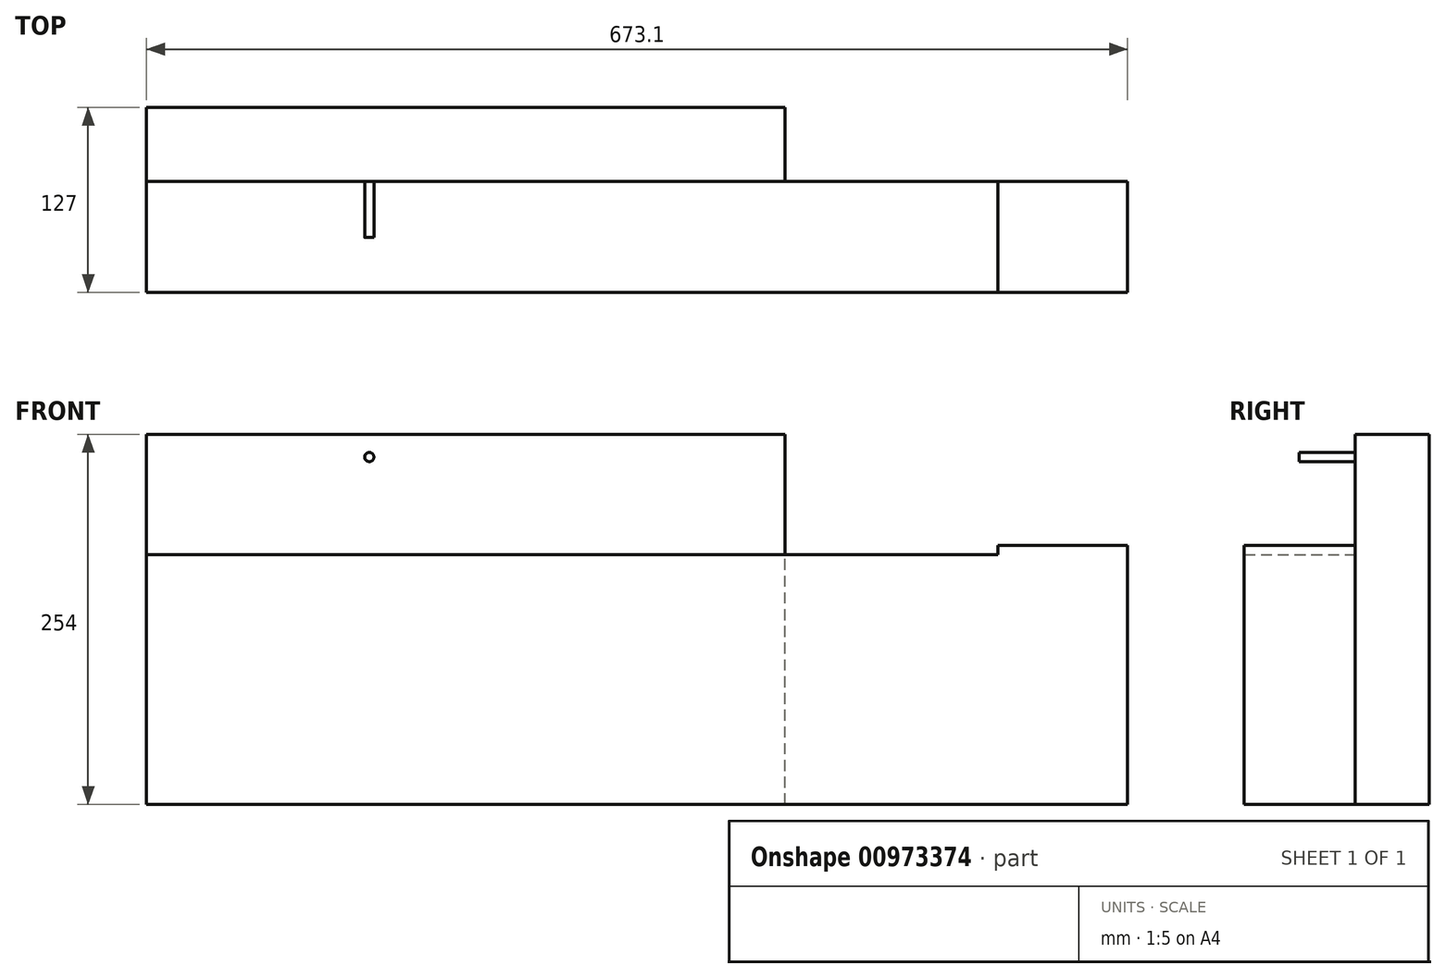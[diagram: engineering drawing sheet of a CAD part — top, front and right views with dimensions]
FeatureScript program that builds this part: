
annotation { "Feature Type Name" : "Feature", "Feature Type Description" : "" }
export const myFeature = defineFeature(function(context is Context, id is Id, definition is map)
    precondition{}
    {
        {
            var Q0;
            Q0=qCreatedBy(makeId("Right.planeOp"),FACE);
            var sketch = newSketch(context, id + "F0", { "sketchPlane" : qUnion([Q0])});
            skLineSegment(sketch, "E0.bottom", {"start": v(-63.5, -127) * mm, "end": v(63.5, -127) * mm});
            skLineSegment(sketch, "E0.top", {"start": v(12.7, 127) * mm, "end": v(63.5, 127) * mm});
            skLineSegment(sketch, "E0.right", {"start": v(63.5, -127) * mm, "end": v(63.5, 127) * mm});
            skPoint(sketch, "E0.middle", {"position": v(0, 0) * mm});
            skLineSegment(sketch, "E1", {"start": v(12.7, 127) * mm, "end": v(12.7, 44.45) * mm});
            skLineSegment(sketch, "E2", {"start": v(12.7, 44.45) * mm, "end": v(-63.5, 44.45) * mm});
            skLineSegment(sketch, "E3", {"start": v(-63.5, 44.45) * mm, "end": v(-63.5, -127) * mm});
            skSolve(sketch);
        }
        {
            var Q0;
            Q0 = qSketchRegion(id + "F0", true);
            extrude(context, id + "F1", {"entities" : qUnion([Q0]), "depth" : 673.1 * mm, "offsetDistance" : 25.4 * mm});
        }
        {
            var Q0;
            Q0=makeQuery(id+"F1.opExtrude","SWEPT_FACE",FACE,{"disambiguationData":[OSD([sQuery(id+"F0.wireOp",EDGE,"E0.top")])]});
            var sketch = newSketch(context, id + "F2", { "sketchPlane" : qUnion([Q0])});
            skLineSegment(sketch, "E4.bottom", {"start": v(673.1, 12.7) * mm, "end": v(438.15, 12.7) * mm});
            skLineSegment(sketch, "E4.top", {"start": v(673.1, 63.5) * mm, "end": v(438.15, 63.5) * mm});
            skLineSegment(sketch, "E4.left", {"start": v(673.1, 12.7) * mm, "end": v(673.1, 63.5) * mm});
            skLineSegment(sketch, "E4.right", {"start": v(438.15, 12.7) * mm, "end": v(438.15, 63.5) * mm});
            skSolve(sketch);
        }
        {
            var Q0;
            Q0 = qSketchRegion(id + "F2", true);
            extrude(context, id + "F3", {"entities" : qUnion([Q0]), "operationType" : NewBodyOperationType.REMOVE, "endBound" : BoundingType.THROUGH_ALL, "oppositeDirection" : true, "depth" : 25.4 * mm, "offsetDistance" : 25.4 * mm});
        }
        {
            var Q0;
            Q0=makeQuery(id+"F1.opExtrude","SWEPT_FACE",FACE,{"disambiguationData":[OSD([sQuery(id+"F0.wireOp",EDGE,"E2")])]});
            var sketch = newSketch(context, id + "F4", { "sketchPlane" : qUnion([Q0])});
            skLineSegment(sketch, "E5.bottom", {"start": v(673.1, -63.5) * mm, "end": v(584.2, -63.5) * mm});
            skLineSegment(sketch, "E5.top", {"start": v(673.1, 12.7) * mm, "end": v(584.2, 12.7) * mm});
            skLineSegment(sketch, "E5.left", {"start": v(673.1, -63.5) * mm, "end": v(673.1, 12.7) * mm});
            skLineSegment(sketch, "E5.right", {"start": v(584.2, -63.5) * mm, "end": v(584.2, 12.7) * mm});
            skSolve(sketch);
        }
        {
            var Q0;
            Q0 = qSketchRegion(id + "F4", true);
            extrude(context, id + "F5", {"entities" : qUnion([Q0]), "operationType" : NewBodyOperationType.ADD, "depth" : 6.35 * mm, "offsetDistance" : 25.4 * mm});
        }
        {
            var Q0;
            Q0=makeQuery(id+"F1.opExtrude","SWEPT_FACE",FACE,{"disambiguationData":[OSD([sQuery(id+"F0.wireOp",EDGE,"E1")])]});
            var sketch = newSketch(context, id + "F6", { "sketchPlane" : qUnion([Q0])});
            skCircle(sketch, "E6", {"center": v(152.78, 111.48) * mm, "radius": 3.18 * mm});
            skSolve(sketch);
        }
        {
            var Q0;
            Q0 = qSketchRegion(id + "F6", true);
            extrude(context, id + "F7", {"entities" : qUnion([Q0]), "operationType" : NewBodyOperationType.ADD, "depth" : 38.53 * mm, "offsetDistance" : 25.4 * mm});
        }
    });
